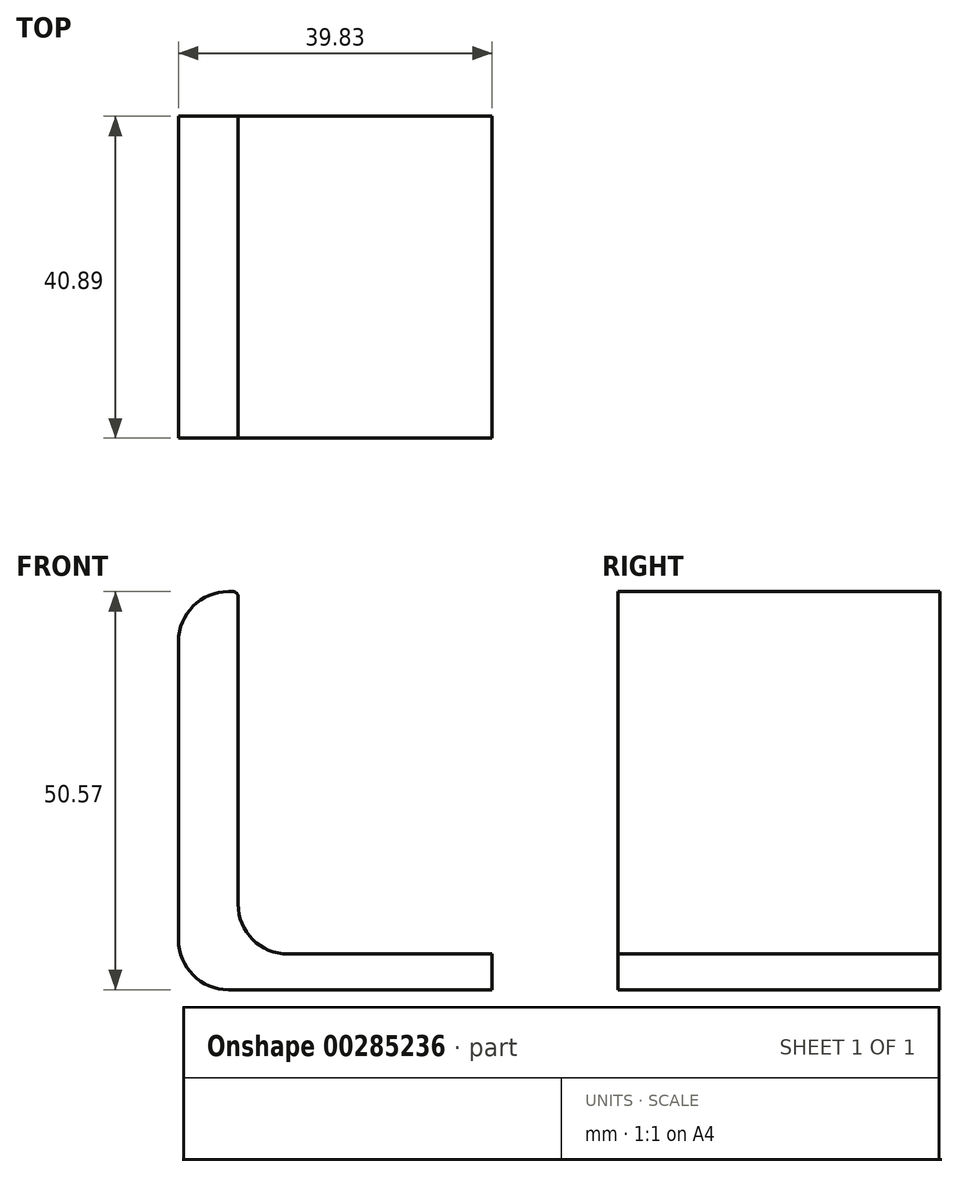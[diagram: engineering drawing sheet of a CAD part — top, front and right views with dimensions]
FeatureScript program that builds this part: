
annotation { "Feature Type Name" : "Feature", "Feature Type Description" : "" }
export const myFeature = defineFeature(function(context is Context, id is Id, definition is map)
    precondition{}
    {
        {
            var Q0;
            Q0=qCreatedBy(makeId("Front.planeOp"),FACE);
            var sketch = newSketch(context, id + "F0", { "sketchPlane" : qUnion([Q0])});
            skLineSegment(sketch, "E0", {"start": v(-26.52, -16.18) * mm, "end": v(25.94, -16.18) * mm});
            skLineSegment(sketch, "E1", {"start": v(25.94, -16.18) * mm, "end": v(25.94, 6.27) * mm});
            skLineSegment(sketch, "E2", {"start": v(25.94, 6.27) * mm, "end": v(-26.52, 21.71) * mm});
            skLineSegment(sketch, "E3", {"start": v(-26.52, -16.18) * mm, "end": v(-26.52, -10.93) * mm});
            skLineSegment(sketch, "E4", {"start": v(-26.52, -10.93) * mm, "end": v(15.8, -10.93) * mm});
            skLineSegment(sketch, "E5", {"start": v(22.15, -4.58) * mm, "end": v(22.15, -1.11) * mm});
            skLineSegment(sketch, "E6", {"start": v(17.59, 4.98) * mm, "end": v(-26.52, 17.93) * mm});
            skLineSegment(sketch, "E7", {"start": v(-26.52, 17.93) * mm, "end": v(-26.52, 21.71) * mm});
            skLineSegment(sketch, "E8", {"start": v(0, 0) * mm, "end": v(-21.05, 0) * mm});
            skLineSegment(sketch, "E9", {"start": v(-27.4, 6.35) * mm, "end": v(-27.4, 44.22) * mm});
            skLineSegment(sketch, "E10", {"start": v(-21.05, 50.57) * mm, "end": v(-20.48, 50.57) * mm});
            skLineSegment(sketch, "E11", {"start": v(-19.82, 49.91) * mm, "end": v(-19.82, 10.87) * mm});
            skLineSegment(sketch, "E12", {"start": v(-13.47, 4.52) * mm, "end": v(0, 4.52) * mm});
            skPoint(sketch, "E13.visualSharp", {"position": v(-19.82, 4.52) * mm});
            skArc(sketch, "E13.filletArc", {"start": v(-19.82, 10.87) * mm, "mid": v(-17.96, 6.38) * mm, "end": v(-13.47, 4.52) * mm});
            skPoint(sketch, "E14.visualSharp", {"position": v(22.15, 3.64) * mm});
            skArc(sketch, "E14.filletArc", {"start": v(22.15, -1.11) * mm, "mid": v(20.89, 2.7) * mm, "end": v(17.59, 4.98) * mm});
            skPoint(sketch, "E15.visualSharp", {"position": v(22.15, -10.93) * mm});
            skArc(sketch, "E15.filletArc", {"start": v(15.8, -10.93) * mm, "mid": v(20.3, -9.07) * mm, "end": v(22.15, -4.58) * mm});
            skPoint(sketch, "E16.visualSharp", {"position": v(-27.4, 0) * mm});
            skArc(sketch, "E16.filletArc", {"start": v(-27.4, 6.35) * mm, "mid": v(-25.54, 1.86) * mm, "end": v(-21.05, 0) * mm});
            skPoint(sketch, "E17.visualSharp", {"position": v(-27.4, 50.57) * mm});
            skArc(sketch, "E17.filletArc", {"start": v(-21.05, 50.57) * mm, "mid": v(-25.54, 48.71) * mm, "end": v(-27.4, 44.22) * mm});
            skPoint(sketch, "E18.visualSharp", {"position": v(-19.82, 50.57) * mm});
            skArc(sketch, "E18.filletArc", {"start": v(-19.82, 49.91) * mm, "mid": v(-20.01, 50.38) * mm, "end": v(-20.48, 50.57) * mm});
            skLineSegment(sketch, "E19", {"start": v(0, 4.52) * mm, "end": v(12.43, 4.52) * mm});
            skLineSegment(sketch, "E20", {"start": v(12.43, 4.52) * mm, "end": v(12.43, 0) * mm});
            skLineSegment(sketch, "E21", {"start": v(12.43, 0) * mm, "end": v(0, 0) * mm});
            skSolve(sketch);
        }
        {
            var Q0;
            {var subQ7=sQuery(id+"F0.wireOp",EDGE,"E7");Q0=makeQuery(id+"F0.imprint","IMPRINT",FACE,{"disambiguationData":[TD([[makeQuery(id+"F0.imprint","IMPRINT",EDGE,{"derivedFrom":subQ7}),1.0]])]});}
            var Q1;
            {var subQ0=sQuery(id+"F0.wireOp",EDGE,"E7");Q1=makeQuery(id+"F0.imprint","IMPRINT",FACE,{"disambiguationData":[TD([[makeQuery(id+"F0.imprint","IMPRINT",EDGE,{"derivedFrom":subQ0}),-1.0]])]});}
            extrude(context, id + "F1", {"entities" : qUnion([Q0, Q1]), "oppositeDirection" : true, "depth" : 40.9 * mm});
        }
    });
